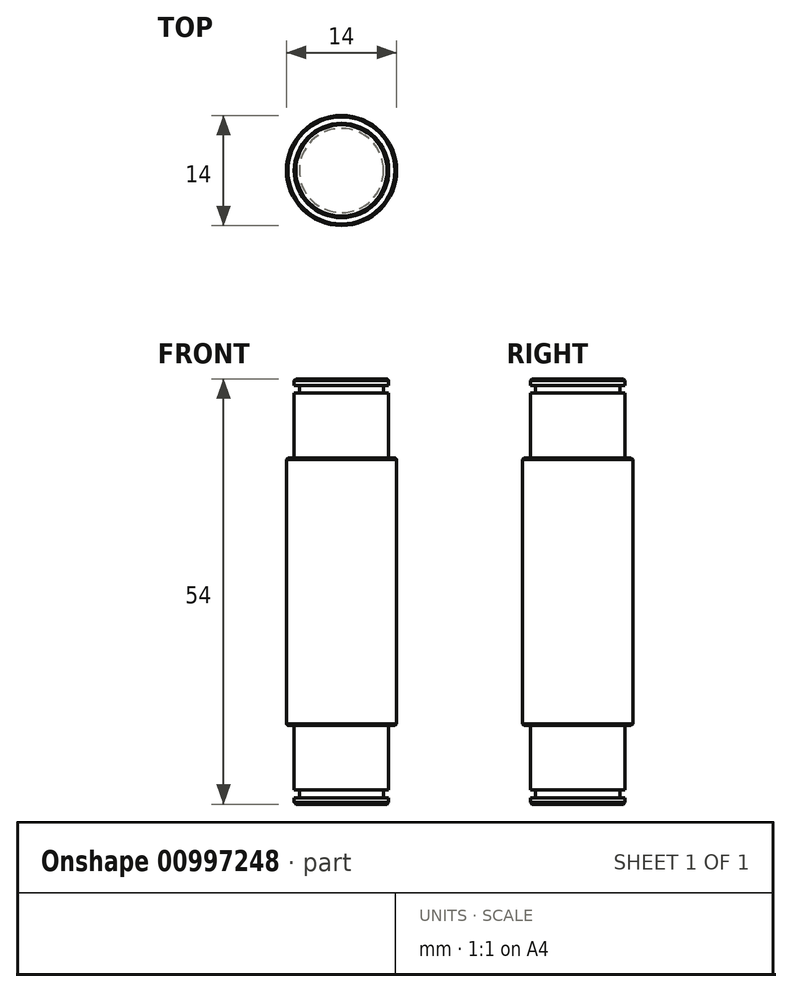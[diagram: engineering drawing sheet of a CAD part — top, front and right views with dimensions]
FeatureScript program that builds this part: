
annotation { "Feature Type Name" : "Feature", "Feature Type Description" : "" }
export const myFeature = defineFeature(function(context is Context, id is Id, definition is map)
    precondition{}
    {
        {
            var Q0;
            Q0=qCreatedBy(makeId("Front.planeOp"),FACE);
            var sketch = newSketch(context, id + "F0", { "sketchPlane" : qUnion([Q0])});
            skLineSegment(sketch, "E0", {"start": v(0, 40.5) * mm, "end": v(0, -44.01) * mm, "construction": true});
            skLineSegment(sketch, "E1", {"start": v(0, 27) * mm, "end": v(-6, 27) * mm});
            skLineSegment(sketch, "E2", {"start": v(-6, 27) * mm, "end": v(-6, 17) * mm});
            skLineSegment(sketch, "E3", {"start": v(-6, 17) * mm, "end": v(-7, 17) * mm});
            skLineSegment(sketch, "E4", {"start": v(-7, 17) * mm, "end": v(-7, -17) * mm});
            skLineSegment(sketch, "E5", {"start": v(-7, -17) * mm, "end": v(-6, -17) * mm});
            skLineSegment(sketch, "E6", {"start": v(-6, -17) * mm, "end": v(-6, -27) * mm});
            skLineSegment(sketch, "E7", {"start": v(-6, -27) * mm, "end": v(0, -27) * mm});
            skLineSegment(sketch, "E8", {"start": v(0, -27) * mm, "end": v(0, 27) * mm});
            skSolve(sketch);
        }
        {
            var Q0;
            Q0 = qSketchRegion(id + "F0", true);
            var Q1;
            Q1=sQuery(id+"F0.wireOp",EDGE,"E0");
            revolve(context, id + "F1", {"surfaceOperationType" : NewSurfaceOperationType.NEW, "entities" : qUnion([Q0]), "axis" : qUnion([Q1]), "revolveType" : RevolveType.FULL});
        }
        {
            var Q0;
            Q0=qCreatedBy(makeId("Front.planeOp"),FACE);
            var sketch = newSketch(context, id + "F2", { "sketchPlane" : qUnion([Q0])});
            skLineSegment(sketch, "E9", {"start": v(-6, 26.2) * mm, "end": v(-5.35, 26.2) * mm});
            skLineSegment(sketch, "E10", {"start": v(-5.35, 26.2) * mm, "end": v(-5.35, 25.2) * mm});
            skLineSegment(sketch, "E11", {"start": v(-5.35, 25.2) * mm, "end": v(-6, 25.2) * mm});
            skLineSegment(sketch, "E12", {"start": v(-6, 26.2) * mm, "end": v(-6, 25.2) * mm});
            skLineSegment(sketch, "E13", {"start": v(0, 31.86) * mm, "end": v(0, -30.42) * mm, "construction": true});
            skLineSegment(sketch, "E14", {"start": v(-13.35, 0) * mm, "end": v(30.09, 0) * mm, "construction": true});
            skLineSegment(sketch, "E15.MirrorCS", {"start": v(-6, -26.2) * mm, "end": v(-5.35, -26.2) * mm});
            skLineSegment(sketch, "E16.MirrorCS", {"start": v(-5.35, -26.2) * mm, "end": v(-5.35, -25.2) * mm});
            skLineSegment(sketch, "E17.MirrorCS", {"start": v(-5.35, -25.2) * mm, "end": v(-6, -25.2) * mm});
            skLineSegment(sketch, "E18.MirrorCS", {"start": v(-6, -26.2) * mm, "end": v(-6, -25.2) * mm});
            skSolve(sketch);
        }
        {
            var Q0;
            Q0 = qSketchRegion(id + "F2", true);
            var Q1;
            Q1=sQuery(id+"F2.wireOp",EDGE,"E13");
            revolve(context, id + "F3", {"operationType" : NewBodyOperationType.REMOVE, "surfaceOperationType" : NewSurfaceOperationType.NEW, "entities" : qUnion([Q0]), "axis" : qUnion([Q1]), "revolveType" : RevolveType.FULL, "oppositeDirection" : true});
        }
        {
            var Q0;
            Q0=makeQuery(id+"F1.opRevolve","SWEPT_EDGE",EDGE,{"disambiguationData":[OSD([sQuery(id+"F0.wireOp",EDGE,"E2"),sQuery(id+"F0.wireOp",EDGE,"E3")])]});
            var Q1;
            Q1=makeQuery(id+"F1.opRevolve","SWEPT_EDGE",EDGE,{"disambiguationData":[OSD([sQuery(id+"F0.wireOp",EDGE,"E5"),sQuery(id+"F0.wireOp",EDGE,"E6")])]});
            fillet(context, id + "F4", {"entities" : qUnion([Q0, Q1]), "radius" : 0.2 * mm, "tangentPropagation" : true, "allowEdgeOverflow" : false});
        }
        {
            var Q0;
            Q0=makeQuery(id+"F1.opRevolve","SWEPT_EDGE",EDGE,{"disambiguationData":[OSD([sQuery(id+"F0.wireOp",EDGE,"E4"),sQuery(id+"F0.wireOp",EDGE,"E5")])]});
            var Q1;
            Q1=makeQuery(id+"F1.opRevolve","SWEPT_EDGE",EDGE,{"disambiguationData":[OSD([sQuery(id+"F0.wireOp",EDGE,"E3"),sQuery(id+"F0.wireOp",EDGE,"E4")])]});
            var Q2;
            Q2=makeQuery(id+"F1.opRevolve","SWEPT_EDGE",EDGE,{"disambiguationData":[OSD([sQuery(id+"F0.wireOp",EDGE,"E1"),sQuery(id+"F0.wireOp",EDGE,"E2")])]});
            var Q3;
            Q3=makeQuery(id+"F1.opRevolve","SWEPT_EDGE",EDGE,{"disambiguationData":[OSD([sQuery(id+"F0.wireOp",EDGE,"E6"),sQuery(id+"F0.wireOp",EDGE,"E7")])]});
            chamfer(context, id + "F5", {"entities" : qUnion([Q0, Q1, Q2, Q3]), "width" : 0.2 * mm, "tangentPropagation" : true});
        }
    });
